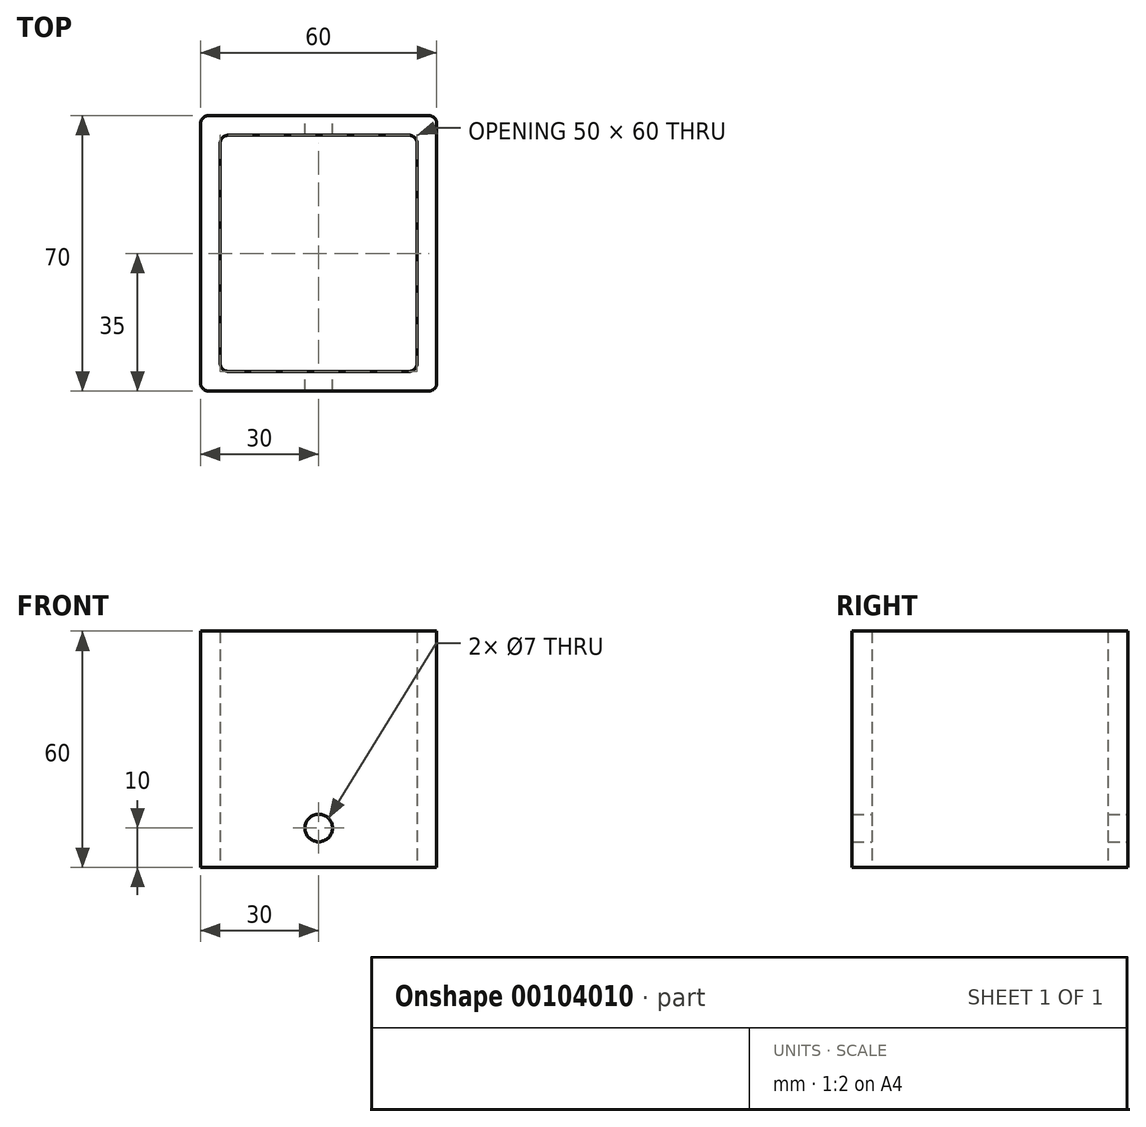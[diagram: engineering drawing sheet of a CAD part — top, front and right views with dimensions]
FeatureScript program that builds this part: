
annotation { "Feature Type Name" : "Feature", "Feature Type Description" : "" }
export const myFeature = defineFeature(function(context is Context, id is Id, definition is map)
    precondition{}
    {
        {
            var Q0;
            Q0=qCreatedBy(makeId("Top.planeOp"),FACE);
            var sketch = newSketch(context, id + "F0", { "sketchPlane" : qUnion([Q0])});
            skLineSegment(sketch, "E0.bottom", {"start": v(30, -35) * mm, "end": v(-30, -35) * mm});
            skLineSegment(sketch, "E0.top", {"start": v(30, 35) * mm, "end": v(-30, 35) * mm});
            skLineSegment(sketch, "E0.left", {"start": v(30, -35) * mm, "end": v(30, 35) * mm});
            skLineSegment(sketch, "E0.right", {"start": v(-30, -35) * mm, "end": v(-30, 35) * mm});
            skPoint(sketch, "E0.middle", {"position": v(0, 0) * mm});
            skLineSegment(sketch, "E1.bottom", {"start": v(-25, 30) * mm, "end": v(25, 30) * mm});
            skLineSegment(sketch, "E1.top", {"start": v(-25, -30) * mm, "end": v(25, -30) * mm});
            skLineSegment(sketch, "E1.left", {"start": v(-25, 30) * mm, "end": v(-25, -30) * mm});
            skLineSegment(sketch, "E1.right", {"start": v(25, 30) * mm, "end": v(25, -30) * mm});
            skSolve(sketch);
        }
        {
            var Q0;
            Q0=makeQuery(id+"F0.imprint","IMPRINT",FACE,{"disambiguationData":[TD([[makeQuery(id+"F0.imprint","IMPRINT",EDGE,{"derivedFrom":sQuery(id+"F0.wireOp",EDGE,"E0.bottom")}),-1.0]])]});
            extrude(context, id + "F1", {"entities" : qUnion([Q0]), "depth" : 60 * mm});
        }
        {
            var Q0;
            Q0=makeQuery(id+"F1.opExtrude","SWEPT_EDGE",EDGE,{"disambiguationData":[OSD([sQuery(id+"F0.wireOp",EDGE,"E0.top"),sQuery(id+"F0.wireOp",EDGE,"E0.right")])]});
            var Q1;
            Q1=makeQuery(id+"F1.opExtrude","SWEPT_EDGE",EDGE,{"disambiguationData":[OSD([sQuery(id+"F0.wireOp",EDGE,"E0.bottom"),sQuery(id+"F0.wireOp",EDGE,"E0.right")])]});
            var Q2;
            Q2=makeQuery(id+"F1.opExtrude","SWEPT_EDGE",EDGE,{"disambiguationData":[OSD([sQuery(id+"F0.wireOp",EDGE,"E0.bottom"),sQuery(id+"F0.wireOp",EDGE,"E0.left")])]});
            var Q3;
            Q3=makeQuery(id+"F1.opExtrude","SWEPT_EDGE",EDGE,{"disambiguationData":[OSD([sQuery(id+"F0.wireOp",EDGE,"E0.top"),sQuery(id+"F0.wireOp",EDGE,"E0.left")])]});
            var Q4;
            Q4=makeQuery(id+"F1.opExtrude","SWEPT_EDGE",EDGE,{"disambiguationData":[OSD([sQuery(id+"F0.wireOp",EDGE,"E1.bottom"),sQuery(id+"F0.wireOp",EDGE,"E1.left")])]});
            var Q5;
            Q5=makeQuery(id+"F1.opExtrude","SWEPT_EDGE",EDGE,{"disambiguationData":[OSD([sQuery(id+"F0.wireOp",EDGE,"E1.top"),sQuery(id+"F0.wireOp",EDGE,"E1.left")])]});
            var Q6;
            Q6=makeQuery(id+"F1.opExtrude","SWEPT_EDGE",EDGE,{"disambiguationData":[OSD([sQuery(id+"F0.wireOp",EDGE,"E1.bottom"),sQuery(id+"F0.wireOp",EDGE,"E1.right")])]});
            var Q7;
            Q7=makeQuery(id+"F1.opExtrude","SWEPT_EDGE",EDGE,{"disambiguationData":[OSD([sQuery(id+"F0.wireOp",EDGE,"E1.top"),sQuery(id+"F0.wireOp",EDGE,"E1.right")])]});
            fillet(context, id + "F2", {"entities" : qUnion([Q0, Q1, Q2, Q3, Q4, Q5, Q6, Q7]), "radius" : 2 * mm, "tangentPropagation" : true, "allowEdgeOverflow" : false});
        }
        {
            var Q0;
            Q0=makeQuery(id+"F1.opExtrude","SWEPT_FACE",FACE,{"disambiguationData":[OSD([sQuery(id+"F0.wireOp",EDGE,"E0.top")])]});
            var sketch = newSketch(context, id + "F3", { "sketchPlane" : qUnion([Q0])});
            skCircle(sketch, "E2", {"center": v(0, 10) * mm, "radius": 3.5 * mm});
            skSolve(sketch);
        }
        {
            var Q0;
            Q0=makeQuery(id+"F3.imprint","IMPRINT",FACE,{"disambiguationData":[TD([[makeQuery(id+"F3.imprint","IMPRINT",EDGE,{"derivedFrom":sQuery(id+"F3.wireOp",EDGE,"E2")}),1.0]])]});
            extrude(context, id + "F4", {"entities" : qUnion([Q0]), "operationType" : NewBodyOperationType.REMOVE, "oppositeDirection" : true, "depth" : 70 * mm});
        }
    });
